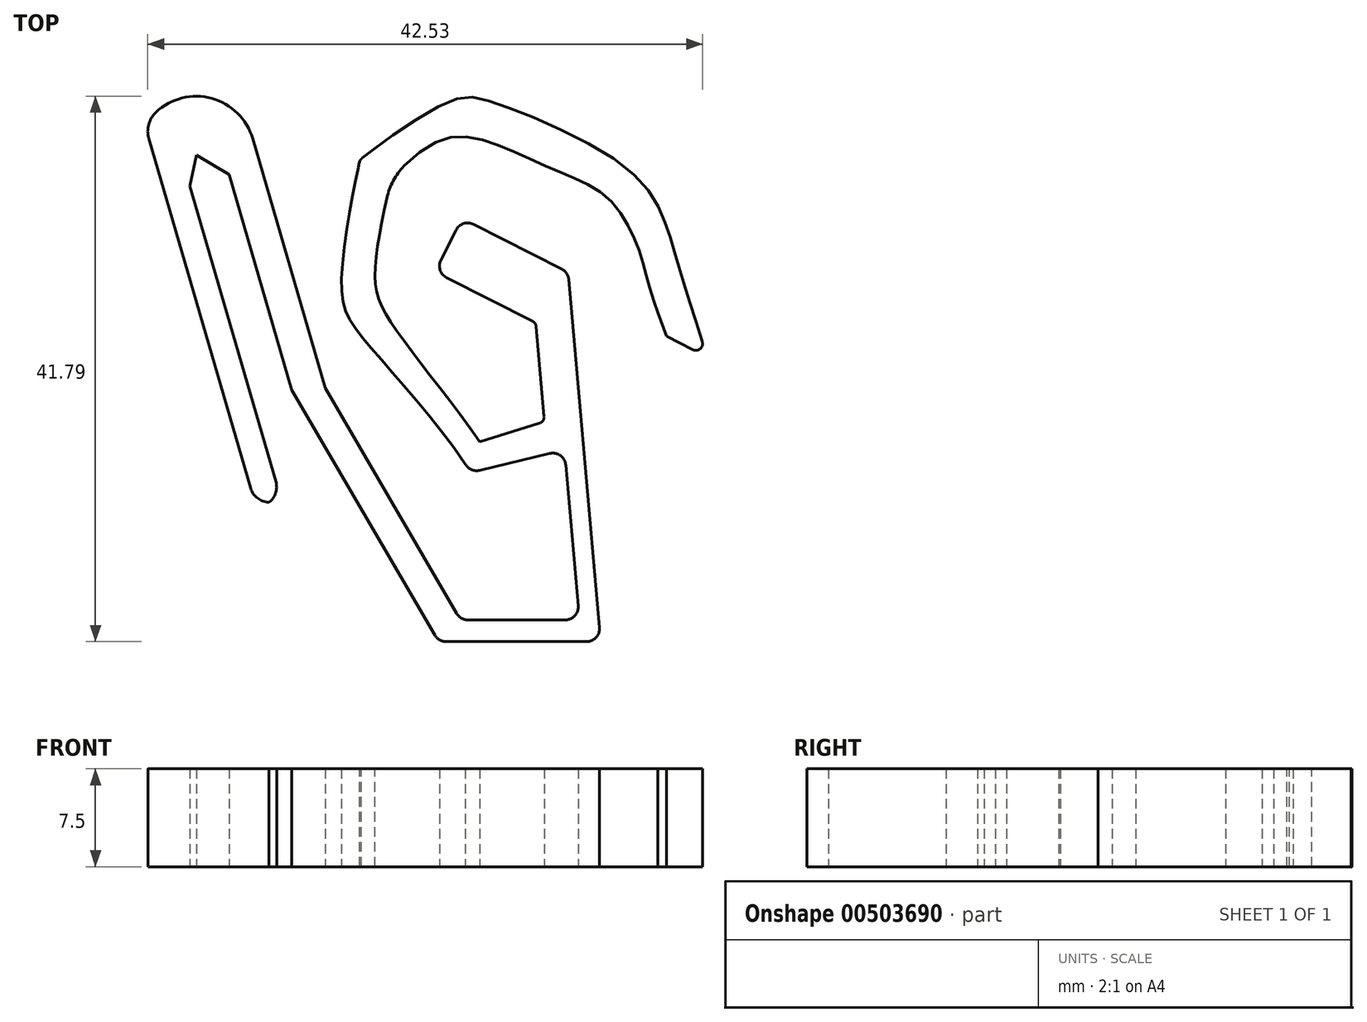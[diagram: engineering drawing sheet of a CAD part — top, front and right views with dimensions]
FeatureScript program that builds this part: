
annotation { "Feature Type Name" : "Feature", "Feature Type Description" : "" }
export const myFeature = defineFeature(function(context is Context, id is Id, definition is map)
    precondition{}
    {
        {
            var Q0;
            Q0=qCreatedBy(makeId("Top.planeOp"),FACE);
            var sketch = newSketch(context, id + "F0", { "sketchPlane" : qUnion([Q0])});
            skLineSegment(sketch, "E0", {"start": v(-27.9, 35.74) * mm, "end": v(-23.1, 19.25) * mm});
            skLineSegment(sketch, "E1", {"start": v(-23.1, 19.25) * mm, "end": v(-12.14, 0.44) * mm});
            skLineSegment(sketch, "E2", {"start": v(-11.28, -0.05) * mm, "end": v(-0.52, -0.05) * mm});
            skLineSegment(sketch, "E3.4", {"start": v(-26.1, 38.5) * mm, "end": v(-20.54, 19.39) * mm});
            skLineSegment(sketch, "E3.5", {"start": v(-20.54, 19.39) * mm, "end": v(-10.47, 2.1) * mm});
            skLineSegment(sketch, "E4", {"start": v(-0.97, 17.4) * mm, "end": v(-1.88, 27.71) * mm});
            skLineSegment(sketch, "E5", {"start": v(-2.42, 28.52) * mm, "end": v(-9.17, 31.93) * mm});
            skLineSegment(sketch, "E6", {"start": v(-10.5, 31.5) * mm, "end": v(-11.68, 29.18) * mm});
            skLineSegment(sketch, "E7", {"start": v(-11.24, 27.84) * mm, "end": v(-4.64, 24.5) * mm});
            skLineSegment(sketch, "E8", {"start": v(-4.37, 24.1) * mm, "end": v(-3.78, 17.42) * mm});
            skLineSegment(sketch, "E9", {"start": v(-4.11, 16.69) * mm, "end": v(-8.7, 15.27) * mm});
            skLineSegment(sketch, "E10", {"start": v(5.6, 23.36) * mm, "end": v(7.66, 22.32) * mm});
            skLineSegment(sketch, "E11", {"start": v(8.36, 22.91) * mm, "end": v(8.34, 22.97) * mm});
            skLineSegment(sketch, "E12.5", {"start": v(-3.33, 14.37) * mm, "end": v(-8.7, 13.07) * mm});
            skLineSegment(sketch, "E13", {"start": v(-0.97, 17.4) * mm, "end": v(-0.55, 12.68) * mm});
            skLineSegment(sketch, "E14", {"start": v(-9.6, 1.61) * mm, "end": v(-2.15, 1.61) * mm});
            skLineSegment(sketch, "E15", {"start": v(-2.1, 13.48) * mm, "end": v(-1.15, 2.7) * mm});
            skPoint(sketch, "E16.visualSharp", {"position": v(-2.2, 14.64) * mm});
            skArc(sketch, "E16.filletArc", {"start": v(-2.1, 13.48) * mm, "mid": v(-2.52, 14.2) * mm, "end": v(-3.33, 14.37) * mm});
            skPoint(sketch, "E17.visualSharp", {"position": v(-1.05, 1.61) * mm});
            skArc(sketch, "E17.filletArc", {"start": v(-2.15, 1.61) * mm, "mid": v(-1.4, 1.94) * mm, "end": v(-1.15, 2.7) * mm});
            skPoint(sketch, "E18.visualSharp", {"position": v(-10.18, 1.61) * mm});
            skArc(sketch, "E18.filletArc", {"start": v(-10.47, 2.1) * mm, "mid": v(-10.1, 1.75) * mm, "end": v(-9.6, 1.61) * mm});
            skPoint(sketch, "E19.visualSharp", {"position": v(-9.43, 12.9) * mm});
            skArc(sketch, "E19.filletArc", {"start": v(-9.8, 13.55) * mm, "mid": v(-9.33, 13.13) * mm, "end": v(-8.7, 13.07) * mm});
            skPoint(sketch, "E20.visualSharp", {"position": v(-1.93, 28.27) * mm});
            skArc(sketch, "E20.filletArc", {"start": v(-1.88, 27.71) * mm, "mid": v(-2.05, 28.18) * mm, "end": v(-2.42, 28.52) * mm});
            skPoint(sketch, "E21.visualSharp", {"position": v(-10.06, 32.38) * mm});
            skArc(sketch, "E21.filletArc", {"start": v(-9.17, 31.93) * mm, "mid": v(-9.93, 32) * mm, "end": v(-10.5, 31.5) * mm});
            skPoint(sketch, "E22.visualSharp", {"position": v(8.7, 21.79) * mm});
            skArc(sketch, "E22.filletArc", {"start": v(7.66, 22.32) * mm, "mid": v(8.2, 22.38) * mm, "end": v(8.36, 22.91) * mm});
            skPoint(sketch, "E23.visualSharp", {"position": v(-12.13, 28.3) * mm});
            skArc(sketch, "E23.filletArc", {"start": v(-11.68, 29.18) * mm, "mid": v(-11.74, 28.42) * mm, "end": v(-11.24, 27.84) * mm});
            skPoint(sketch, "E24.visualSharp", {"position": v(-8.7, 15.27) * mm});
            skPoint(sketch, "E25.visualSharp", {"position": v(-3.73, 16.8) * mm});
            skArc(sketch, "E25.filletArc", {"start": v(-4.11, 16.69) * mm, "mid": v(-3.84, 16.89) * mm, "end": v(-3.76, 17.21) * mm});
            skPoint(sketch, "E26.visualSharp", {"position": v(-4.4, 24.37) * mm});
            skArc(sketch, "E26.filletArc", {"start": v(-4.37, 24.1) * mm, "mid": v(-4.45, 24.33) * mm, "end": v(-4.64, 24.5) * mm});
            skPoint(sketch, "E27.visualSharp", {"position": v(-17.89, 36.88) * mm});
            skArc(sketch, "E27.filletArc", {"start": v(-17.7, 37) * mm, "mid": v(-17.85, 36.85) * mm, "end": v(-17.92, 36.66) * mm});
            skPoint(sketch, "E28.visualSharp", {"position": v(-15.51, 35.35) * mm});
            skFitSpline(sketch, "E29", {"points": [v(-15.51, 35.35) * mm, v(-16.73, 28.06) * mm, v(-15.7, 24.74) * mm, v(-8.7, 15.27) * mm], "startDerivative": vector(-5.19, -24.34) * mm, "endDerivative": vector(18.21, -26.22) * mm});
            skFitSpline(sketch, "E30.0", {"points": [v(-15.51, 35.35) * mm, v(-15.04, 35.83) * mm, v(-14.1, 36.8) * mm, v(-12.86, 37.79) * mm, v(-11.8, 38.33) * mm, v(-10.96, 38.59) * mm, v(-10.07, 38.65) * mm, v(-9.11, 38.54) * mm, v(-8.12, 38.29) * mm, v(-7.1, 37.93) * mm, v(-6.09, 37.5) * mm, v(-5.07, 37.04) * mm, v(-4.1, 36.58) * mm, v(-3.15, 36.17) * mm, v(-2.26, 35.8) * mm, v(-1.44, 35.47) * mm, v(-0.67, 35.12) * mm, v(0.04, 34.75) * mm, v(0.69, 34.31) * mm, v(1.28, 33.79) * mm, v(1.8, 33.18) * mm, v(2.28, 32.51) * mm, v(2.69, 31.82) * mm, v(3.03, 31.14) * mm, v(3.3, 30.5) * mm, v(3.52, 29.92) * mm, v(3.7, 29.35) * mm, v(3.87, 28.73) * mm, v(4.03, 28.13) * mm, v(4.2, 27.58) * mm, v(4.37, 26.98) * mm, v(4.63, 26.15) * mm, v(4.84, 25.48) * mm, v(4.94, 25.16) * mm]});
            skLineSegment(sketch, "E31", {"start": v(4.94, 25.16) * mm, "end": v(5.6, 23.36) * mm});
            skFitSpline(sketch, "E32", {"points": [v(8.34, 22.97) * mm, v(6.7, 28.3) * mm, v(5.63, 31.72) * mm, v(2.75, 36.07) * mm, v(-7.35, 41.18) * mm, v(-11.36, 41.2) * mm, v(-17.7, 37) * mm, v(-17.92, 36.66) * mm, v(-19.3, 27.87) * mm, v(-17.99, 23.66) * mm, v(-9.8, 13.55) * mm], "startDerivative": vector(-18.09, 57.37) * mm, "endDerivative": vector(55.8, -82.88) * mm});
            skLineSegment(sketch, "E33.0", {"start": v(-34.35, 39.46) * mm, "end": v(-25.83, 10.21) * mm});
            skArc(sketch, "E34", {"start": v(-26.1, 38.5) * mm, "mid": v(-29.9, 41.7) * mm, "end": v(-34.35, 39.46) * mm});
            skLineSegment(sketch, "E35", {"start": v(-30.43, 37.24) * mm, "end": v(-30.92, 34.85) * mm});
            skLineSegment(sketch, "E36.MirrorCS", {"start": v(-30.43, 37.24) * mm, "end": v(-27.9, 35.74) * mm});
            skLineSegment(sketch, "E37", {"start": v(-30.92, 34.85) * mm, "end": v(-23.93, 10.84) * mm});
            skLineSegment(sketch, "E38", {"start": v(-25.83, 10.21) * mm, "end": v(-24.88, 10.53) * mm});
            skLineSegment(sketch, "E39", {"start": v(-26.77, 17.72) * mm, "end": v(-26.77, 17.72) * mm});
            skPoint(sketch, "E40", {"position": v(-24.88, 10.53) * mm});
            skLineSegment(sketch, "E41", {"start": v(-24.88, 10.53) * mm, "end": v(-23.93, 10.84) * mm});
            skLineSegment(sketch, "E42", {"start": v(-0.55, 12.68) * mm, "end": v(0.48, 1.03) * mm});
            skLineSegment(sketch, "E43", {"start": v(-5.66, 24.4) * mm, "end": v(-5.66, 24.4) * mm});
            skLineSegment(sketch, "E44", {"start": v(-3.78, 17.42) * mm, "end": v(-3.76, 17.21) * mm});
            skPoint(sketch, "E45.visualSharp", {"position": v(0.58, -0.05) * mm});
            skArc(sketch, "E45.filletArc", {"start": v(-0.52, -0.05) * mm, "mid": v(0.22, 0.27) * mm, "end": v(0.48, 1.03) * mm});
            skPoint(sketch, "E46.visualSharp", {"position": v(-11.85, -0.05) * mm});
            skArc(sketch, "E46.filletArc", {"start": v(-12.14, 0.44) * mm, "mid": v(-11.78, 0.08) * mm, "end": v(-11.28, -0.05) * mm});
            skSolve(sketch);
        }
        {
            var Q0;
            Q0=makeQuery(id+"F0.imprint","IMPRINT",FACE,{"disambiguationData":[TD([[makeQuery(id+"F0.imprint","IMPRINT",EDGE,{"derivedFrom":sQuery(id+"F0.wireOp",EDGE,"E0")}),1.0]])]});
            extrude(context, id + "F1", {"entities" : qUnion([Q0]), "depth" : 7.5 * mm});
        }
        {
            var Q0;
            Q0=makeQuery(id+"F1.opExtrude","SWEPT_EDGE",EDGE,{"disambiguationData":[OSD([sQuery(id+"F0.wireOp",EDGE,"E33.0"),sQuery(id+"F0.wireOp",EDGE,"E38")])]});
            var Q1;
            Q1=makeQuery(id+"F1.opExtrude","SWEPT_EDGE",EDGE,{"disambiguationData":[OSD([sQuery(id+"F0.wireOp",EDGE,"E37"),sQuery(id+"F0.wireOp",EDGE,"E41")])]});
            fillet(context, id + "F2", {"entities" : qUnion([Q0, Q1]), "radius" : 1.5 * mm, "tangentPropagation" : true, "allowEdgeOverflow" : false});
        }
        {
            var Q0;
            Q0=makeQuery(id+"F1.opExtrude","SWEPT_EDGE",EDGE,{"disambiguationData":[OSD([sQuery(id+"F0.wireOp",EDGE,"E29"),sQuery(id+"F0.wireOp",EDGE,"E30.0")])]});
            fillet(context, id + "F3", {"entities" : qUnion([Q0]), "radius" : 5 * mm, "tangentPropagation" : true, "allowEdgeOverflow" : false});
        }
        {
            var Q0;
            Q0=makeQuery(id+"F1.opExtrude","SWEPT_EDGE",EDGE,{"disambiguationData":[OSD([sQuery(id+"F0.wireOp",EDGE,"E33.0"),sQuery(id+"F0.wireOp",EDGE,"E34")])]});
            fillet(context, id + "F4", {"entities" : qUnion([Q0]), "radius" : 2 * mm, "tangentPropagation" : true, "allowEdgeOverflow" : false});
        }
    });
